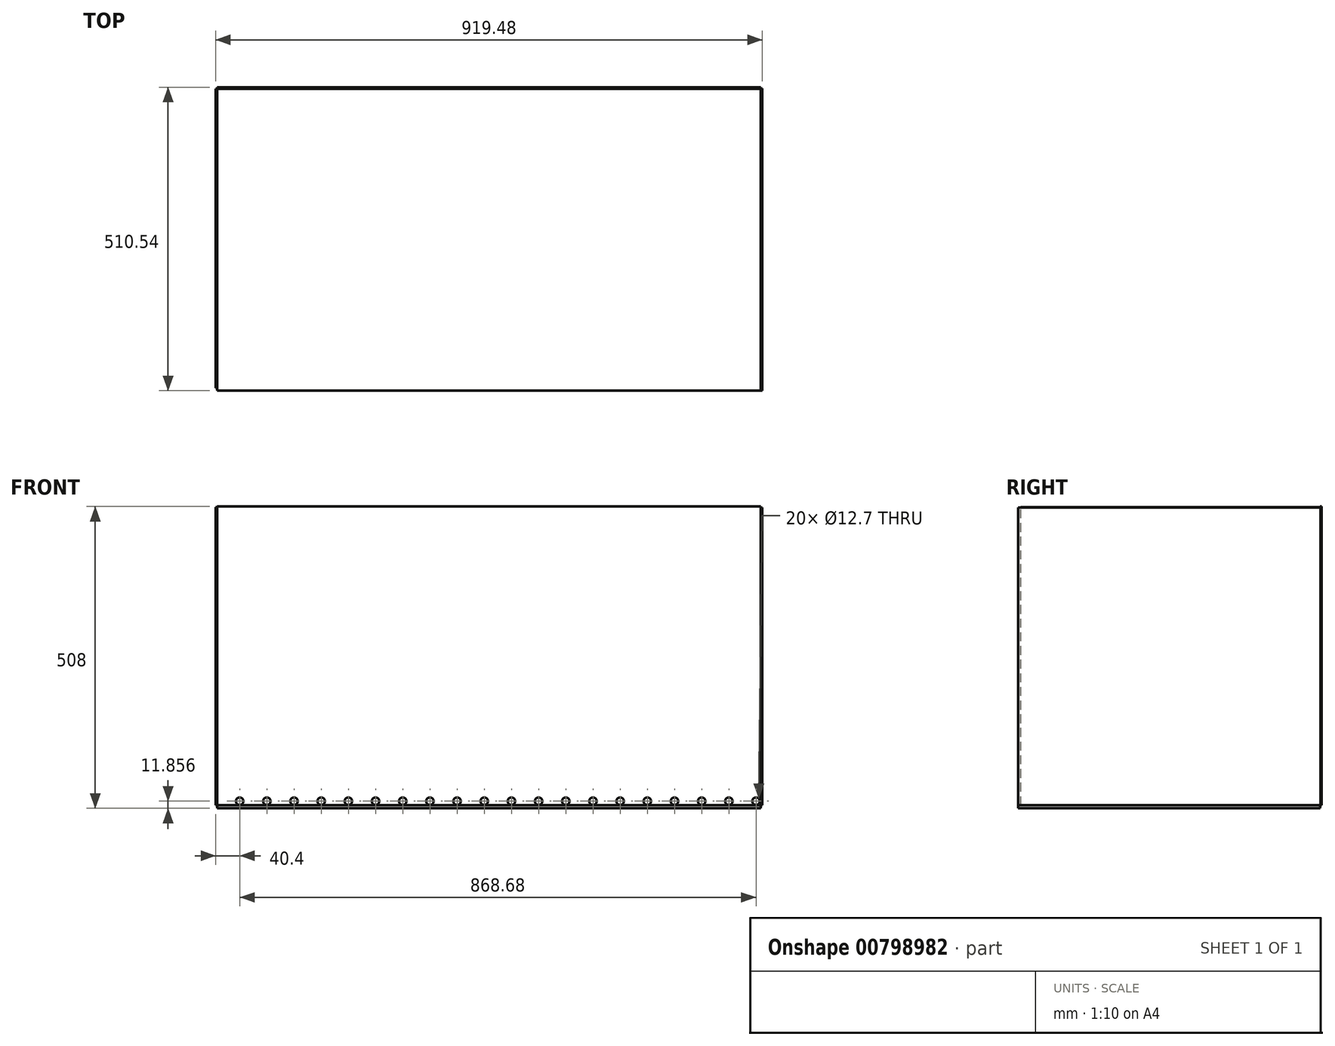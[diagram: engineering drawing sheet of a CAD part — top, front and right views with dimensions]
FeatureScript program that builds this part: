
annotation { "Feature Type Name" : "Feature", "Feature Type Description" : "" }
export const myFeature = defineFeature(function(context is Context, id is Id, definition is map)
    precondition{}
    {
        {
            var Q0;
            Q0=qCreatedBy(makeId("Top.planeOp"),FACE);
            var sketch = newSketch(context, id + "F0", { "sketchPlane" : qUnion([Q0])});
            skLineSegment(sketch, "E0.bottom", {"start": v(457.2, 254) * mm, "end": v(-457.2, 254) * mm});
            skLineSegment(sketch, "E0.top", {"start": v(457.2, -254) * mm, "end": v(-457.2, -254) * mm});
            skLineSegment(sketch, "E0.left", {"start": v(457.2, 254) * mm, "end": v(457.2, -254) * mm});
            skLineSegment(sketch, "E0.right", {"start": v(-457.2, 254) * mm, "end": v(-457.2, -254) * mm});
            skPoint(sketch, "E0.middle", {"position": v(0, 0) * mm});
            skPoint(sketch, "E1", {"position": v(-457.2, 254) * mm});
            skPoint(sketch, "E2", {"position": v(457.2, 254) * mm});
            skPoint(sketch, "E3", {"position": v(-457.2, -254) * mm});
            skPoint(sketch, "E4", {"position": v(457.2, -254) * mm});
            skSolve(sketch);
        }
        {
            var Q0;
            Q0=makeQuery(id+"F0.imprint","IMPRINT",FACE,{"disambiguationData":[TD([[makeQuery(id+"F0.imprint","IMPRINT",EDGE,{"derivedFrom":sQuery(id+"F0.wireOp",EDGE,"E0.bottom")}),1.0]])]});
            extrude(context, id + "F1", {"entities" : qUnion([Q0]), "depth" : 5.08 * mm, "offsetDistance" : 25.4 * mm});
        }
        {
            var Q0;
            Q0=makeQuery(id+"F1.opExtrude","SWEPT_FACE",FACE,{"disambiguationData":[OSD([sQuery(id+"F0.wireOp",EDGE,"E0.bottom")])]});
            var sketch = newSketch(context, id + "F2", { "sketchPlane" : qUnion([Q0])});
            skLineSegment(sketch, "E5.bottom", {"start": v(-457.2, 0) * mm, "end": v(457.2, 0) * mm});
            skLineSegment(sketch, "E5.top", {"start": v(-457.2, 0) * mm, "end": v(457.2, 0) * mm});
            skLineSegment(sketch, "E5.left", {"start": v(-457.2, 0) * mm, "end": v(-457.2, 0) * mm});
            skLineSegment(sketch, "E5.right", {"start": v(457.2, 0) * mm, "end": v(457.2, 0) * mm});
            skLineSegment(sketch, "E6.top", {"start": v(-457.2, 508) * mm, "end": v(457.2, 508) * mm});
            skLineSegment(sketch, "E6.left", {"start": v(-457.2, 0) * mm, "end": v(-457.2, 508) * mm});
            skLineSegment(sketch, "E6.right", {"start": v(457.2, 0) * mm, "end": v(457.2, 508) * mm});
            skSolve(sketch);
        }
        {
            var Q0;
            {var subQ0=sQuery(id+"F2.wireOp",EDGE,"E6.top");Q0=makeQuery(id+"F2.imprint","IMPRINT",FACE,{"disambiguationData":[TD([[makeQuery(id+"F2.imprint","IMPRINT",EDGE,{"derivedFrom":subQ0}),-1.0]])]});}
            extrude(context, id + "F3", {"entities" : qUnion([Q0]), "depth" : 2.54 * mm, "offsetDistance" : 25.4 * mm});
        }
        {
            var Q0;
            Q0=makeQuery(id+"F1.opExtrude","SWEPT_FACE",FACE,{"disambiguationData":[OSD([sQuery(id+"F0.wireOp",EDGE,"E0.right")])]});
            var sketch = newSketch(context, id + "F4", { "sketchPlane" : qUnion([Q0])});
            skLineSegment(sketch, "E7.bottom", {"start": v(-254, 5.08) * mm, "end": v(249.46, 5.08) * mm});
            skLineSegment(sketch, "E7.top", {"start": v(-254, 507.08) * mm, "end": v(249.46, 507.08) * mm});
            skLineSegment(sketch, "E7.left", {"start": v(-254, 5.08) * mm, "end": v(-254, 507.08) * mm});
            skLineSegment(sketch, "E7.right", {"start": v(249.46, 5.08) * mm, "end": v(249.46, 507.08) * mm});
            skSolve(sketch);
        }
        {
            var Q0;
            Q0=makeQuery(id+"F4.imprint","IMPRINT",FACE,{"disambiguationData":[TD([[makeQuery(id+"F4.imprint","IMPRINT",EDGE,{"derivedFrom":sQuery(id+"F4.wireOp",EDGE,"E7.bottom")}),1.0]])]});
            extrude(context, id + "F5", {"entities" : qUnion([Q0]), "depth" : 2.54 * mm, "offsetDistance" : 25.4 * mm});
        }
        {
            var Q0;
            Q0=makeQuery(id+"F1.opExtrude","SWEPT_FACE",FACE,{"disambiguationData":[OSD([sQuery(id+"F0.wireOp",EDGE,"E0.left")])]});
            var sketch = newSketch(context, id + "F6", { "sketchPlane" : qUnion([Q0])});
            skLineSegment(sketch, "E8.bottom", {"start": v(-254, 5.08) * mm, "end": v(254.54, 5.08) * mm});
            skLineSegment(sketch, "E8.top", {"start": v(-254, 506.13) * mm, "end": v(254.54, 506.13) * mm});
            skLineSegment(sketch, "E8.left", {"start": v(-254, 5.08) * mm, "end": v(-254, 506.13) * mm});
            skLineSegment(sketch, "E8.right", {"start": v(254.54, 5.08) * mm, "end": v(254.54, 506.13) * mm});
            skSolve(sketch);
        }
        {
            var Q0;
            Q0=makeQuery(id+"F6.imprint","IMPRINT",FACE,{"disambiguationData":[TD([[makeQuery(id+"F6.imprint","IMPRINT",EDGE,{"derivedFrom":sQuery(id+"F6.wireOp",EDGE,"E8.top")}),-1.0]])]});
            extrude(context, id + "F7", {"entities" : qUnion([Q0]), "operationType" : NewBodyOperationType.ADD, "depth" : 2.54 * mm, "offsetDistance" : 25.4 * mm});
        }
        {
            var Q0;
            Q0=makeQuery(id+"F3.opExtrude","CAP_FACE",FACE,{"disambiguationData":[OSD([sQuery(id+"F0.wireOp",EDGE,"E0.bottom"),sQuery(id+"F2.wireOp",EDGE,"E6.top"),sQuery(id+"F2.wireOp",EDGE,"E6.left"),sQuery(id+"F2.wireOp",EDGE,"E6.right")])],"isStart":false});
            var sketch = newSketch(context, id + "F8", { "sketchPlane" : qUnion([Q0])});
            skCircle(sketch, "E9", {"center": v(-449.34, 11.86) * mm, "radius": 5.21 * mm});
            skCircle(sketch, "E10.1.0.0", {"center": v(-403.62, 11.86) * mm, "radius": 5.21 * mm});
            skCircle(sketch, "E10.2.0.0", {"center": v(-357.9, 11.86) * mm, "radius": 5.21 * mm});
            skCircle(sketch, "E10.3.0.0", {"center": v(-312.18, 11.86) * mm, "radius": 5.21 * mm});
            skCircle(sketch, "E10.4.0.0", {"center": v(-266.46, 11.86) * mm, "radius": 5.21 * mm});
            skCircle(sketch, "E10.5.0.0", {"center": v(-220.74, 11.86) * mm, "radius": 5.21 * mm});
            skCircle(sketch, "E10.6.0.0", {"center": v(-175.02, 11.86) * mm, "radius": 5.21 * mm});
            skCircle(sketch, "E10.7.0.0", {"center": v(-129.3, 11.86) * mm, "radius": 5.21 * mm});
            skCircle(sketch, "E10.8.0.0", {"center": v(-83.58, 11.86) * mm, "radius": 5.21 * mm});
            skCircle(sketch, "E10.9.0.0", {"center": v(-37.86, 11.86) * mm, "radius": 5.21 * mm});
            skCircle(sketch, "E10.10.0.0", {"center": v(7.86, 11.86) * mm, "radius": 5.21 * mm});
            skCircle(sketch, "E10.11.0.0", {"center": v(53.58, 11.86) * mm, "radius": 5.21 * mm});
            skCircle(sketch, "E10.12.0.0", {"center": v(99.3, 11.86) * mm, "radius": 5.21 * mm});
            skCircle(sketch, "E10.13.0.0", {"center": v(145.02, 11.86) * mm, "radius": 5.21 * mm});
            skCircle(sketch, "E10.14.0.0", {"center": v(190.74, 11.86) * mm, "radius": 5.21 * mm});
            skCircle(sketch, "E10.15.0.0", {"center": v(236.46, 11.86) * mm, "radius": 5.21 * mm});
            skCircle(sketch, "E10.16.0.0", {"center": v(282.18, 11.86) * mm, "radius": 5.21 * mm});
            skCircle(sketch, "E10.17.0.0", {"center": v(327.9, 11.86) * mm, "radius": 5.21 * mm});
            skCircle(sketch, "E10.18.0.0", {"center": v(373.62, 11.86) * mm, "radius": 5.21 * mm});
            skCircle(sketch, "E10.19.0.0", {"center": v(419.34, 11.86) * mm, "radius": 5.21 * mm});
            skLineSegment(sketch, "E10.direction1", {"start": v(-449.34, 11.86) * mm, "end": v(-403.62, 11.86) * mm, "construction": true});
            skSolve(sketch);
        }
        {
            var Q0;
            Q0=sQuery(id+"F8.wireOp",VERTEX,"E10.direction1.end");
            var Q1;
            Q1=sQuery(id+"F8.wireOp",VERTEX,"E10.direction1.start");
            var Q2;
            Q2=sQuery(id+"F8.wireOp",VERTEX,"E10.2.0.0.center");
            var Q3;
            Q3=sQuery(id+"F8.wireOp",VERTEX,"E10.3.0.0.center");
            var Q4;
            Q4=sQuery(id+"F8.wireOp",VERTEX,"E10.4.0.0.center");
            var Q5;
            Q5=sQuery(id+"F8.wireOp",VERTEX,"E10.5.0.0.center");
            var Q6;
            Q6=sQuery(id+"F8.wireOp",VERTEX,"E10.6.0.0.center");
            var Q7;
            Q7=sQuery(id+"F8.wireOp",VERTEX,"E10.7.0.0.center");
            var Q8;
            Q8=sQuery(id+"F8.wireOp",VERTEX,"E10.8.0.0.center");
            var Q9;
            Q9=sQuery(id+"F8.wireOp",VERTEX,"E10.9.0.0.center");
            var Q10;
            Q10=sQuery(id+"F8.wireOp",VERTEX,"E10.10.0.0.center");
            var Q11;
            Q11=sQuery(id+"F8.wireOp",VERTEX,"E10.11.0.0.center");
            var Q12;
            Q12=sQuery(id+"F8.wireOp",VERTEX,"E10.12.0.0.center");
            var Q13;
            Q13=sQuery(id+"F8.wireOp",VERTEX,"E10.13.0.0.center");
            var Q14;
            Q14=sQuery(id+"F8.wireOp",VERTEX,"E10.14.0.0.center");
            var Q15;
            Q15=sQuery(id+"F8.wireOp",VERTEX,"E10.15.0.0.center");
            var Q16;
            Q16=sQuery(id+"F8.wireOp",VERTEX,"E10.16.0.0.center");
            var Q17;
            Q17=sQuery(id+"F8.wireOp",VERTEX,"E10.17.0.0.center");
            var Q18;
            Q18=sQuery(id+"F8.wireOp",VERTEX,"E10.18.0.0.center");
            var Q19;
            Q19=sQuery(id+"F8.wireOp",VERTEX,"E10.19.0.0.center");
            var Q20;
            Q20=makeQuery(id+"F3.opExtrude","SWEPT_BODY",BODY,{"disambiguationData":[OSD([sQuery(id+"F0.wireOp",EDGE,"E0.bottom"),sQuery(id+"F2.wireOp",EDGE,"E6.top"),sQuery(id+"F2.wireOp",EDGE,"E6.left"),sQuery(id+"F2.wireOp",EDGE,"E6.right")])]});
            hole(context, id + "F9", {"style" : HoleStyle.SIMPLE, "endStyle" : HoleEndStyle.BLIND, "holeDiameter" : 12.7 * mm, "majorDiameter" : 6.35 * mm, "holeDepth" : 7.37 * mm, "isTappedThrough" : true, "tappedDepth" : 12.7 * mm, "tapClearance" : 3, "startFromSketch" : true, "locations" : qUnion([Q0, Q1, Q2, Q3, Q4, Q5, Q6, Q7, Q8, Q9, Q10, Q11, Q12, Q13, Q14, Q15, Q16, Q17, Q18, Q19]), "scope" : qUnion([Q20])});
        }
    });
